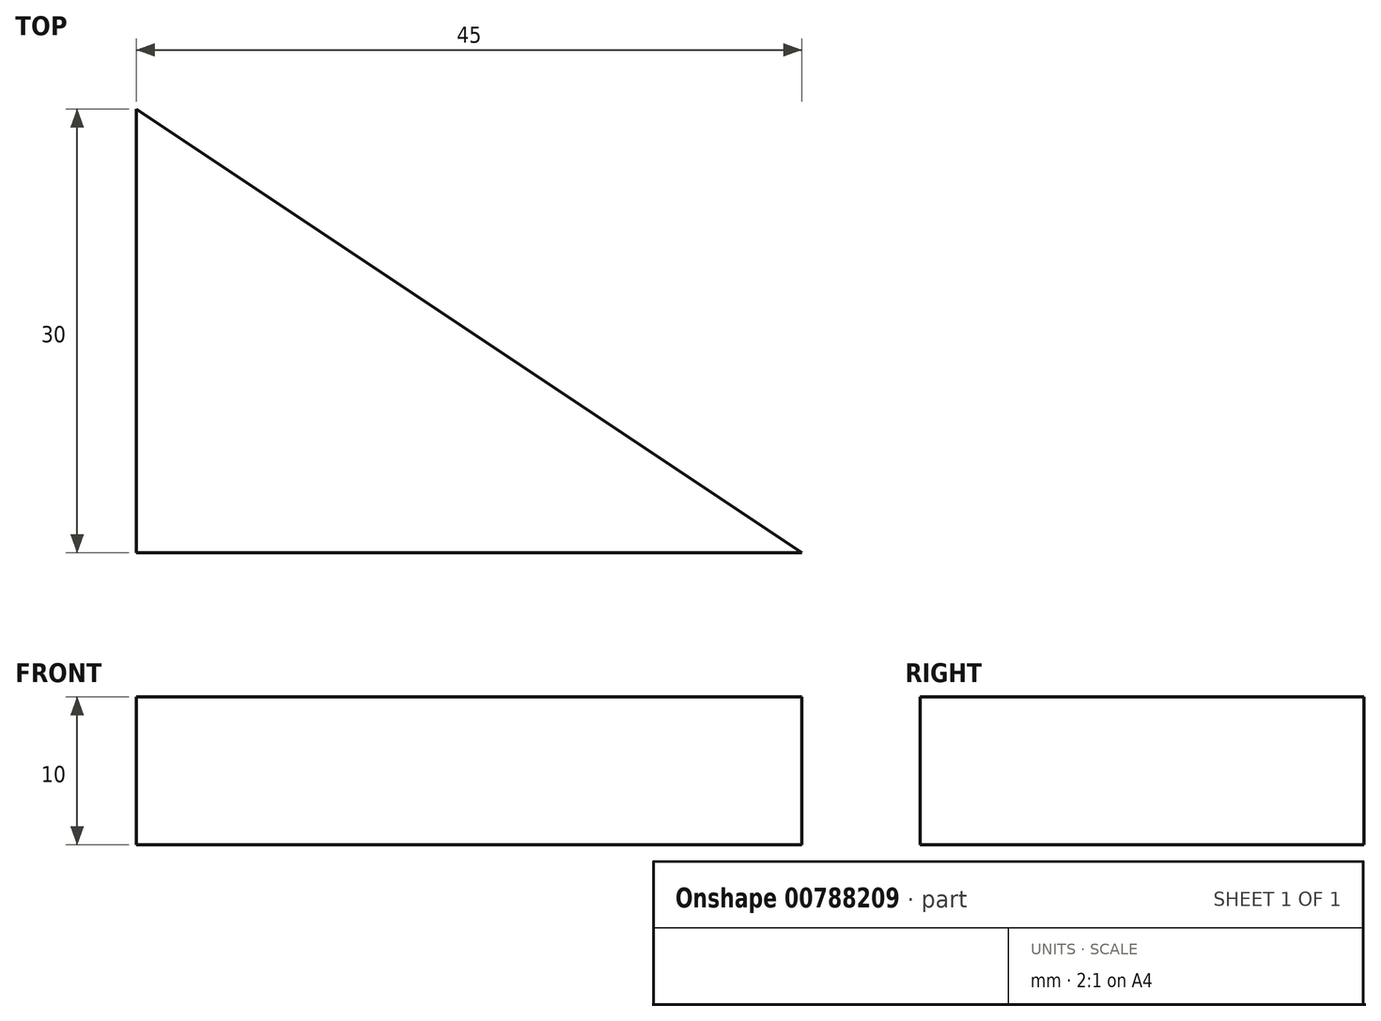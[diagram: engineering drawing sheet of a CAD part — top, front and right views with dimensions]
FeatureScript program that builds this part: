
annotation { "Feature Type Name" : "Feature", "Feature Type Description" : "" }
export const myFeature = defineFeature(function(context is Context, id is Id, definition is map)
    precondition{}
    {
        {
            var Q0;
            Q0=qCreatedBy(makeId("Top.planeOp"),FACE);
            var sketch = newSketch(context, id + "F0", { "sketchPlane" : qUnion([Q0])});
            skLineSegment(sketch, "E0", {"start": v(0, 0) * mm, "end": v(0, 30) * mm});
            skLineSegment(sketch, "E1", {"start": v(0, 30) * mm, "end": v(45, 0) * mm});
            skLineSegment(sketch, "E2", {"start": v(45, 0) * mm, "end": v(0, 0) * mm});
            skSolve(sketch);
        }
        {
            var Q0;
            Q0 = qSketchRegion(id + "F0", true);
            extrude(context, id + "F1", {"entities" : qUnion([Q0]), "depth" : 10 * mm, "offsetDistance" : 25 * mm});
        }
    });
